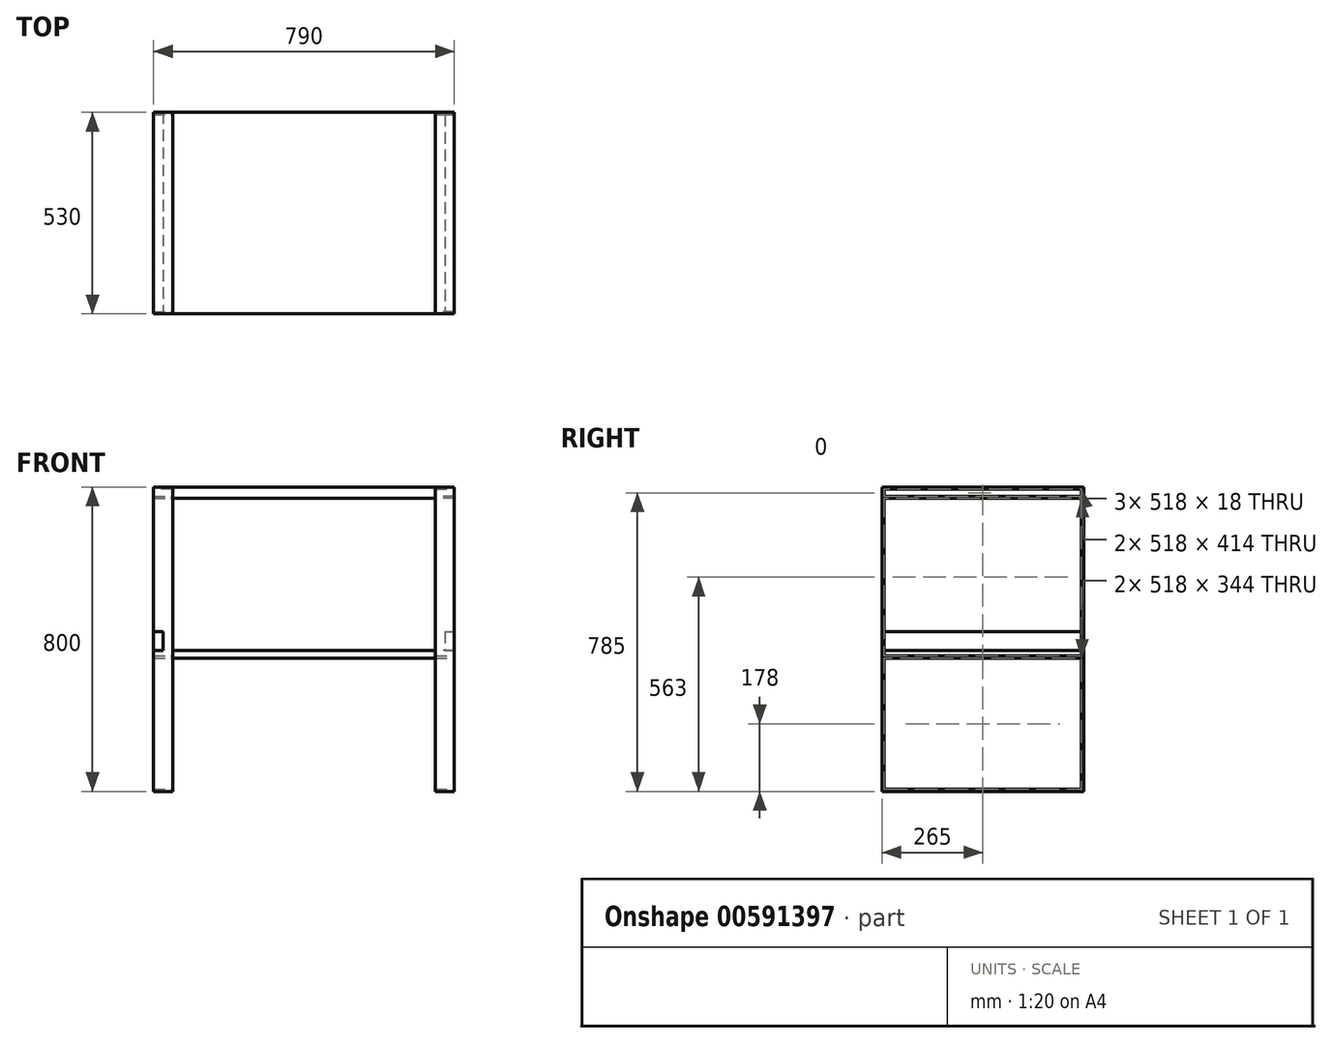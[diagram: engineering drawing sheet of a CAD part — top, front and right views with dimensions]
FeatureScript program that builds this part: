
annotation { "Feature Type Name" : "Feature", "Feature Type Description" : "" }
export const myFeature = defineFeature(function(context is Context, id is Id, definition is map)
    precondition{}
    {
        {
            assignVariable(context, id + "F0", {"name" : "largeur", "anyValue" : 790});
        }
        {
            assignVariable(context, id + "F1", {"name" : "hauteur", "anyValue" : 800});
        }
        {
            var Q0;
            Q0=qCreatedBy(makeId("Top.planeOp"),FACE);
            var sketch = newSketch(context, id + "F2", { "sketchPlane" : qUnion([Q0])});
            skLineSegment(sketch, "E0.bottom", {"start": v(-395, -259) * mm, "end": v(-345, -259) * mm});
            skLineSegment(sketch, "E0.top", {"start": v(-395, -265) * mm, "end": v(-345, -265) * mm});
            skLineSegment(sketch, "E0.left", {"start": v(-395, -259) * mm, "end": v(-395, -265) * mm});
            skLineSegment(sketch, "E0.right", {"start": v(-345, -259) * mm, "end": v(-345, -265) * mm});
            skLineSegment(sketch, "E1.MirrorCS", {"start": v(-345, 259) * mm, "end": v(-345, 265) * mm});
            skLineSegment(sketch, "E2.MirrorCS", {"start": v(-395, 259) * mm, "end": v(-395, 265) * mm});
            skLineSegment(sketch, "E3.MirrorCS", {"start": v(-395, 265) * mm, "end": v(-345, 265) * mm});
            skLineSegment(sketch, "E4.MirrorCS", {"start": v(-395, 259) * mm, "end": v(-345, 259) * mm});
            skLineSegment(sketch, "E5.MirrorCS", {"start": v(345, -259) * mm, "end": v(345, -265) * mm});
            skLineSegment(sketch, "E6.MirrorCS", {"start": v(395, 259) * mm, "end": v(395, 265) * mm});
            skLineSegment(sketch, "E7.MirrorCS", {"start": v(345, 259) * mm, "end": v(345, 265) * mm});
            skLineSegment(sketch, "E8.MirrorCS", {"start": v(395, -259) * mm, "end": v(395, -265) * mm});
            skLineSegment(sketch, "E9.MirrorCS", {"start": v(395, -259) * mm, "end": v(345, -259) * mm});
            skLineSegment(sketch, "E10.MirrorCS", {"start": v(395, -265) * mm, "end": v(345, -265) * mm});
            skLineSegment(sketch, "E11.MirrorCS", {"start": v(395, 265) * mm, "end": v(345, 265) * mm});
            skLineSegment(sketch, "E12.MirrorCS", {"start": v(395, 259) * mm, "end": v(345, 259) * mm});
            skSolve(sketch);
        }
        {
            var Q0;
            Q0=qSketchRegion(id+"F2",true);
            extrude(context, id + "F3", {"entities" : qUnion([Q0]), "depth" : (getVariable(context, 'hauteur')) * mm});
        }
        {
            var Q0;
            Q0=makeQuery(id+"F3.opExtrude","SWEPT_FACE",FACE,{"disambiguationData":[OSD([sQuery(id+"F2.wireOp",EDGE,"E9.MirrorCS")])]});
            var sketch = newSketch(context, id + "F4", { "sketchPlane" : qUnion([Q0])});
            skLineSegment(sketch, "E13.bottom", {"start": v(-345, 800) * mm, "end": v(-395, 800) * mm});
            skLineSegment(sketch, "E13.top", {"start": v(-345, 794) * mm, "end": v(-395, 794) * mm});
            skLineSegment(sketch, "E13.left", {"start": v(-345, 800) * mm, "end": v(-345, 794) * mm});
            skLineSegment(sketch, "E13.right", {"start": v(-395, 800) * mm, "end": v(-395, 794) * mm});
            skLineSegment(sketch, "E14.bottom", {"start": v(-395, 776) * mm, "end": v(-345, 776) * mm});
            skLineSegment(sketch, "E14.top", {"start": v(-395, 770) * mm, "end": v(-345, 770) * mm});
            skLineSegment(sketch, "E14.left", {"start": v(-395, 776) * mm, "end": v(-395, 770) * mm});
            skLineSegment(sketch, "E14.right", {"start": v(-345, 776) * mm, "end": v(-345, 770) * mm});
            skLineSegment(sketch, "E15.MirrorCS", {"start": v(345, 776) * mm, "end": v(345, 770) * mm});
            skLineSegment(sketch, "E16.MirrorCS", {"start": v(395, 776) * mm, "end": v(345, 776) * mm});
            skLineSegment(sketch, "E17.MirrorCS", {"start": v(395, 776) * mm, "end": v(395, 770) * mm});
            skLineSegment(sketch, "E18.MirrorCS", {"start": v(395, 770) * mm, "end": v(345, 770) * mm});
            skLineSegment(sketch, "E19.MirrorCS", {"start": v(395, 800) * mm, "end": v(395, 794) * mm});
            skLineSegment(sketch, "E20.MirrorCS", {"start": v(345, 800) * mm, "end": v(395, 800) * mm});
            skLineSegment(sketch, "E21.MirrorCS", {"start": v(345, 794) * mm, "end": v(395, 794) * mm});
            skLineSegment(sketch, "E22.MirrorCS", {"start": v(345, 800) * mm, "end": v(345, 794) * mm});
            skLineSegment(sketch, "E23.bottom", {"start": v(-395, 0) * mm, "end": v(-345, 0) * mm});
            skLineSegment(sketch, "E23.top", {"start": v(-395, 6) * mm, "end": v(-345, 6) * mm});
            skLineSegment(sketch, "E23.left", {"start": v(-395, 0) * mm, "end": v(-395, 6) * mm});
            skLineSegment(sketch, "E23.right", {"start": v(-345, 0) * mm, "end": v(-345, 6) * mm});
            skLineSegment(sketch, "E24.MirrorCS", {"start": v(395, 0) * mm, "end": v(395, 6) * mm});
            skLineSegment(sketch, "E25.MirrorCS", {"start": v(395, 6) * mm, "end": v(345, 6) * mm});
            skLineSegment(sketch, "E26.MirrorCS", {"start": v(395, 0) * mm, "end": v(345, 0) * mm});
            skLineSegment(sketch, "E27.MirrorCS", {"start": v(345, 0) * mm, "end": v(345, 6) * mm});
            skLineSegment(sketch, "E28.bottom", {"start": v(-395, 356) * mm, "end": v(-345, 356) * mm});
            skLineSegment(sketch, "E28.top", {"start": v(-395, 350) * mm, "end": v(-345, 350) * mm});
            skLineSegment(sketch, "E28.left", {"start": v(-395, 356) * mm, "end": v(-395, 350) * mm});
            skLineSegment(sketch, "E28.right", {"start": v(-345, 356) * mm, "end": v(-345, 350) * mm});
            skLineSegment(sketch, "E29.MirrorCS", {"start": v(395, 356) * mm, "end": v(395, 350) * mm});
            skLineSegment(sketch, "E30.MirrorCS", {"start": v(395, 350) * mm, "end": v(345, 350) * mm});
            skLineSegment(sketch, "E31.MirrorCS", {"start": v(345, 356) * mm, "end": v(345, 350) * mm});
            skLineSegment(sketch, "E32.MirrorCS", {"start": v(395, 356) * mm, "end": v(345, 356) * mm});
            skSolve(sketch);
        }
        {
            var Q0;
            Q0=qSketchRegion(id+"F4",true);
            extrude(context, id + "F5", {"entities" : qUnion([Q0]), "endBound" : BoundingType.UP_TO_NEXT, "depth" : 25 * mm});
        }
        {
            var Q0;
            Q0=makeQuery(id+"F3.opExtrude","SWEPT_BODY",BODY,{"disambiguationData":[OSD([sQuery(id+"F2.wireOp",EDGE,"E5.MirrorCS"),sQuery(id+"F2.wireOp",EDGE,"E8.MirrorCS"),sQuery(id+"F2.wireOp",EDGE,"E9.MirrorCS"),sQuery(id+"F2.wireOp",EDGE,"E10.MirrorCS")])]});
            var Q1;
            Q1=makeQuery(id+"F5.opExtrude","SWEPT_BODY",BODY,{"disambiguationData":[OSD([sQuery(id+"F4.wireOp",EDGE,"E13.bottom"),sQuery(id+"F4.wireOp",EDGE,"E13.top"),sQuery(id+"F4.wireOp",EDGE,"E13.left"),sQuery(id+"F4.wireOp",EDGE,"E13.right")])]});
            var Q2;
            Q2=makeQuery(id+"F5.opExtrude","SWEPT_BODY",BODY,{"disambiguationData":[OSD([sQuery(id+"F4.wireOp",EDGE,"E14.bottom"),sQuery(id+"F4.wireOp",EDGE,"E14.top"),sQuery(id+"F4.wireOp",EDGE,"E14.left"),sQuery(id+"F4.wireOp",EDGE,"E14.right")])]});
            var Q3;
            Q3=makeQuery(id+"F3.opExtrude","SWEPT_BODY",BODY,{"disambiguationData":[OSD([sQuery(id+"F2.wireOp",EDGE,"E6.MirrorCS"),sQuery(id+"F2.wireOp",EDGE,"E7.MirrorCS"),sQuery(id+"F2.wireOp",EDGE,"E11.MirrorCS"),sQuery(id+"F2.wireOp",EDGE,"E12.MirrorCS")])]});
            booleanBodies(context, id + "F6", {"operationType" : BooleanOperationType.UNION, "tools" : qUnion([Q0, Q1, Q2, Q3])});
        }
        {
            var Q0;
            Q0=makeQuery(id+"F3.opExtrude","SWEPT_BODY",BODY,{"disambiguationData":[OSD([sQuery(id+"F2.wireOp",EDGE,"E0.bottom"),sQuery(id+"F2.wireOp",EDGE,"E0.top"),sQuery(id+"F2.wireOp",EDGE,"E0.left"),sQuery(id+"F2.wireOp",EDGE,"E0.right")])]});
            var Q1;
            Q1=makeQuery(id+"F3.opExtrude","SWEPT_BODY",BODY,{"disambiguationData":[OSD([sQuery(id+"F2.wireOp",EDGE,"E1.MirrorCS"),sQuery(id+"F2.wireOp",EDGE,"E2.MirrorCS"),sQuery(id+"F2.wireOp",EDGE,"E3.MirrorCS"),sQuery(id+"F2.wireOp",EDGE,"E4.MirrorCS")])]});
            var Q2;
            Q2=makeQuery(id+"F5.opExtrude","SWEPT_BODY",BODY,{"disambiguationData":[OSD([sQuery(id+"F4.wireOp",EDGE,"E15.MirrorCS"),sQuery(id+"F4.wireOp",EDGE,"E16.MirrorCS"),sQuery(id+"F4.wireOp",EDGE,"E17.MirrorCS"),sQuery(id+"F4.wireOp",EDGE,"E18.MirrorCS")])]});
            var Q3;
            Q3=makeQuery(id+"F5.opExtrude","SWEPT_BODY",BODY,{"disambiguationData":[OSD([sQuery(id+"F4.wireOp",EDGE,"E19.MirrorCS"),sQuery(id+"F4.wireOp",EDGE,"E20.MirrorCS"),sQuery(id+"F4.wireOp",EDGE,"E21.MirrorCS"),sQuery(id+"F4.wireOp",EDGE,"E22.MirrorCS")])]});
            booleanBodies(context, id + "F7", {"operationType" : BooleanOperationType.UNION, "tools" : qUnion([Q0, Q1, Q2, Q3])});
        }
        {
            var Q0;
            Q0=makeQuery(id+"F5.opExtrude","SWEPT_BODY",BODY,{"disambiguationData":[OSD([sQuery(id+"F4.wireOp",EDGE,"E28.bottom"),sQuery(id+"F4.wireOp",EDGE,"E28.top"),sQuery(id+"F4.wireOp",EDGE,"E28.left"),sQuery(id+"F4.wireOp",EDGE,"E28.right")])]});
            var Q1;
            Q1=makeQuery(id+"F5.opExtrude","SWEPT_BODY",BODY,{"disambiguationData":[OSD([sQuery(id+"F4.wireOp",EDGE,"E23.bottom"),sQuery(id+"F4.wireOp",EDGE,"E23.top"),sQuery(id+"F4.wireOp",EDGE,"E23.left"),sQuery(id+"F4.wireOp",EDGE,"E23.right")])]});
            var Q2;
            Q2=makeQuery(id+"F3.opExtrude","SWEPT_BODY",BODY,{"disambiguationData":[OSD([sQuery(id+"F2.wireOp",EDGE,"E5.MirrorCS"),sQuery(id+"F2.wireOp",EDGE,"E8.MirrorCS"),sQuery(id+"F2.wireOp",EDGE,"E9.MirrorCS"),sQuery(id+"F2.wireOp",EDGE,"E10.MirrorCS")])]});
            booleanBodies(context, id + "F8", {"operationType" : BooleanOperationType.UNION, "tools" : qUnion([Q0, Q1, Q2])});
        }
        {
            var Q0;
            Q0=makeQuery(id+"F5.opExtrude","SWEPT_BODY",BODY,{"disambiguationData":[OSD([sQuery(id+"F4.wireOp",EDGE,"E29.MirrorCS"),sQuery(id+"F4.wireOp",EDGE,"E30.MirrorCS"),sQuery(id+"F4.wireOp",EDGE,"E31.MirrorCS"),sQuery(id+"F4.wireOp",EDGE,"E32.MirrorCS")])]});
            var Q1;
            Q1=makeQuery(id+"F5.opExtrude","SWEPT_BODY",BODY,{"disambiguationData":[OSD([sQuery(id+"F4.wireOp",EDGE,"E24.MirrorCS"),sQuery(id+"F4.wireOp",EDGE,"E25.MirrorCS"),sQuery(id+"F4.wireOp",EDGE,"E26.MirrorCS"),sQuery(id+"F4.wireOp",EDGE,"E27.MirrorCS")])]});
            var Q2;
            Q2=makeQuery(id+"F3.opExtrude","SWEPT_BODY",BODY,{"disambiguationData":[OSD([sQuery(id+"F2.wireOp",EDGE,"E0.bottom"),sQuery(id+"F2.wireOp",EDGE,"E0.top"),sQuery(id+"F2.wireOp",EDGE,"E0.left"),sQuery(id+"F2.wireOp",EDGE,"E0.right")])]});
            booleanBodies(context, id + "F9", {"operationType" : BooleanOperationType.UNION, "tools" : qUnion([Q0, Q1, Q2])});
        }
        {
            var Q0;
            Q0=qCreatedBy(makeId("Right.planeOp"),FACE);
            var sketch = newSketch(context, id + "F10", { "sketchPlane" : qUnion([Q0])});
            skLineSegment(sketch, "E33.bottom", {"start": v(265, 800) * mm, "end": v(-265, 800) * mm});
            skLineSegment(sketch, "E33.top", {"start": v(265, 770) * mm, "end": v(-265, 770) * mm});
            skLineSegment(sketch, "E33.left", {"start": v(265, 800) * mm, "end": v(265, 770) * mm});
            skLineSegment(sketch, "E33.right", {"start": v(-265, 800) * mm, "end": v(-265, 770) * mm});
            skLineSegment(sketch, "E34.bottom", {"start": v(265, 370) * mm, "end": v(-265, 370) * mm});
            skLineSegment(sketch, "E34.top", {"start": v(265, 350) * mm, "end": v(-265, 350) * mm});
            skLineSegment(sketch, "E34.left", {"start": v(265, 370) * mm, "end": v(265, 350) * mm});
            skLineSegment(sketch, "E34.right", {"start": v(-265, 370) * mm, "end": v(-265, 350) * mm});
            skSolve(sketch);
        }
        {
            var Q0;
            Q0=qSketchRegion(id+"F10",true);
            extrude(context, id + "F11", {"entities" : qUnion([Q0]), "depth" : (getVariable(context, 'largeur') / 2) * mm, "hasSecondDirection" : true, "secondDirectionOppositeDirection" : true, "secondDirectionDepth" : (getVariable(context, 'largeur') / 2) * mm});
        }
        {
            var Q0;
            Q0=makeQuery(id+"F5.opExtrude","SWEPT_BODY",BODY,{"disambiguationData":[OSD([sQuery(id+"F4.wireOp",EDGE,"E29.MirrorCS"),sQuery(id+"F4.wireOp",EDGE,"E30.MirrorCS"),sQuery(id+"F4.wireOp",EDGE,"E31.MirrorCS"),sQuery(id+"F4.wireOp",EDGE,"E32.MirrorCS")])]});
            var Q1;
            Q1=makeQuery(id+"F5.opExtrude","SWEPT_BODY",BODY,{"disambiguationData":[OSD([sQuery(id+"F4.wireOp",EDGE,"E28.bottom"),sQuery(id+"F4.wireOp",EDGE,"E28.top"),sQuery(id+"F4.wireOp",EDGE,"E28.left"),sQuery(id+"F4.wireOp",EDGE,"E28.right")])]});
            var Q2;
            Q2=makeQuery(id+"F11.opExtrude","SWEPT_BODY",BODY,{"disambiguationData":[OSD([sQuery(id+"F10.wireOp",EDGE,"E34.bottom"),sQuery(id+"F10.wireOp",EDGE,"E34.top"),sQuery(id+"F10.wireOp",EDGE,"E34.left"),sQuery(id+"F10.wireOp",EDGE,"E34.right")])]});
            booleanBodies(context, id + "F12", {"operationType" : BooleanOperationType.SUBTRACTION, "tools" : qUnion([Q0, Q1]), "targets" : qUnion([Q2]), "keepTools" : true});
        }
        {
            var Q0;
            Q0=makeQuery(id+"F5.opExtrude","SWEPT_BODY",BODY,{"disambiguationData":[OSD([sQuery(id+"F4.wireOp",EDGE,"E29.MirrorCS"),sQuery(id+"F4.wireOp",EDGE,"E30.MirrorCS"),sQuery(id+"F4.wireOp",EDGE,"E31.MirrorCS"),sQuery(id+"F4.wireOp",EDGE,"E32.MirrorCS")])]});
            var Q1;
            Q1=makeQuery(id+"F5.opExtrude","SWEPT_BODY",BODY,{"disambiguationData":[OSD([sQuery(id+"F4.wireOp",EDGE,"E28.bottom"),sQuery(id+"F4.wireOp",EDGE,"E28.top"),sQuery(id+"F4.wireOp",EDGE,"E28.left"),sQuery(id+"F4.wireOp",EDGE,"E28.right")])]});
            var Q2;
            Q2=makeQuery(id+"F11.opExtrude","SWEPT_BODY",BODY,{"disambiguationData":[OSD([sQuery(id+"F10.wireOp",EDGE,"E33.bottom"),sQuery(id+"F10.wireOp",EDGE,"E33.top"),sQuery(id+"F10.wireOp",EDGE,"E33.left"),sQuery(id+"F10.wireOp",EDGE,"E33.right")])]});
            booleanBodies(context, id + "F13", {"operationType" : BooleanOperationType.SUBTRACTION, "tools" : qUnion([Q0, Q1]), "targets" : qUnion([Q2]), "keepTools" : true});
        }
        {
            var Q0;
            Q0=makeQuery(id+"F11.opExtrude","SWEPT_FACE",FACE,{"disambiguationData":[OSD([sQuery(id+"F10.wireOp",EDGE,"E34.bottom")])]});
            var sketch = newSketch(context, id + "F14", { "sketchPlane" : qUnion([Q0])});
            skPoint(sketch, "E35.oppositeSnap0", {"position": v(370, -259) * mm});
            skLineSegment(sketch, "E35.bottom", {"start": v(395, 265) * mm, "end": v(370, 265) * mm});
            skLineSegment(sketch, "E35.top", {"start": v(395, -265) * mm, "end": v(370, -265) * mm});
            skLineSegment(sketch, "E35.left", {"start": v(395, 265) * mm, "end": v(395, -265) * mm});
            skLineSegment(sketch, "E35.right", {"start": v(370, 265) * mm, "end": v(370, -265) * mm});
            skPoint(sketch, "E36.MirrorP", {"position": v(-370, -259) * mm});
            skLineSegment(sketch, "E37.MirrorCS", {"start": v(-395, 265) * mm, "end": v(-395, -265) * mm});
            skLineSegment(sketch, "E38.MirrorCS", {"start": v(-370, 265) * mm, "end": v(-370, -265) * mm});
            skLineSegment(sketch, "E39.MirrorCS", {"start": v(-395, 265) * mm, "end": v(-370, 265) * mm});
            skLineSegment(sketch, "E40.MirrorCS", {"start": v(-395, -265) * mm, "end": v(-370, -265) * mm});
            skSolve(sketch);
        }
        {
            var Q0;
            Q0=qSketchRegion(id+"F14",true);
            extrude(context, id + "F15", {"entities" : qUnion([Q0]), "depth" : 50 * mm, "offsetDistance" : 25 * mm});
        }
        {
            var Q0;
            Q0=makeQuery(id+"F5.opExtrude","SWEPT_BODY",BODY,{"disambiguationData":[OSD([sQuery(id+"F4.wireOp",EDGE,"E28.bottom"),sQuery(id+"F4.wireOp",EDGE,"E28.top"),sQuery(id+"F4.wireOp",EDGE,"E28.left"),sQuery(id+"F4.wireOp",EDGE,"E28.right")])]});
            var Q1;
            Q1=makeQuery(id+"F5.opExtrude","SWEPT_BODY",BODY,{"disambiguationData":[OSD([sQuery(id+"F4.wireOp",EDGE,"E29.MirrorCS"),sQuery(id+"F4.wireOp",EDGE,"E30.MirrorCS"),sQuery(id+"F4.wireOp",EDGE,"E31.MirrorCS"),sQuery(id+"F4.wireOp",EDGE,"E32.MirrorCS")])]});
            var Q2;
            Q2=makeQuery(id+"F15.opExtrude","SWEPT_BODY",BODY,{"disambiguationData":[OSD([sQuery(id+"F14.wireOp",EDGE,"E35.bottom"),sQuery(id+"F14.wireOp",EDGE,"E35.top"),sQuery(id+"F14.wireOp",EDGE,"E35.left"),sQuery(id+"F14.wireOp",EDGE,"E35.right")])]});
            booleanBodies(context, id + "F16", {"operationType" : BooleanOperationType.SUBTRACTION, "tools" : qUnion([Q0, Q1]), "targets" : qUnion([Q2]), "keepTools" : true});
        }
    });
